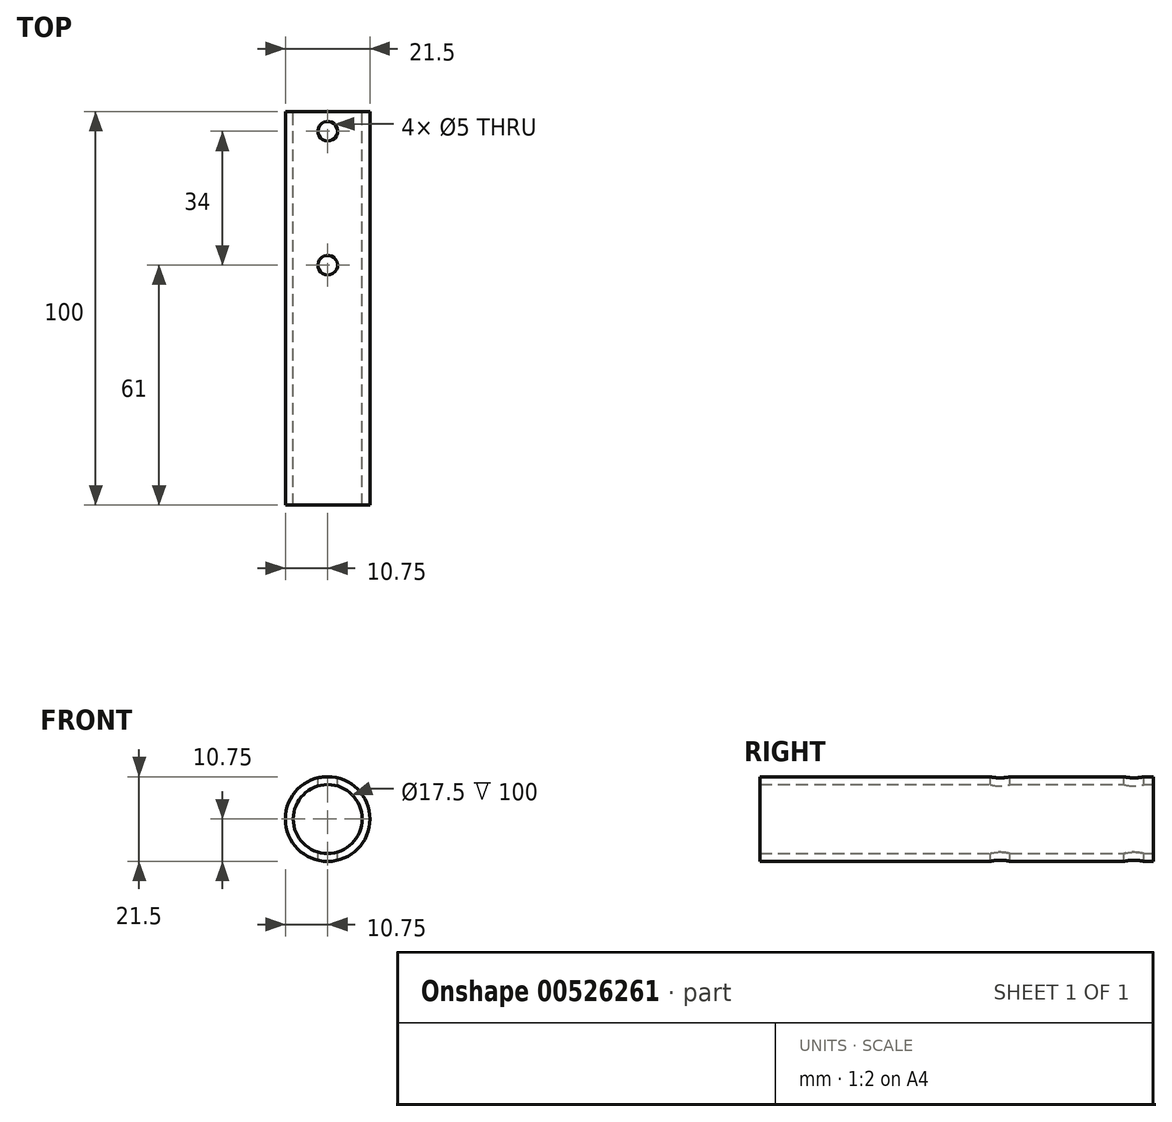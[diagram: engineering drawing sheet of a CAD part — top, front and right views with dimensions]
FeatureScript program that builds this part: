
annotation { "Feature Type Name" : "Feature", "Feature Type Description" : "" }
export const myFeature = defineFeature(function(context is Context, id is Id, definition is map)
    precondition{}
    {
        {
            var Q0;
            Q0=qCreatedBy(makeId("Front.planeOp"),FACE);
            var sketch = newSketch(context, id + "F0", { "sketchPlane" : qUnion([Q0])});
            skCircle(sketch, "E0", {"center": v(0, 0) * mm, "radius": 10.75 * mm});
            skCircle(sketch, "E1", {"center": v(0, 0) * mm, "radius": 8.75 * mm});
            skSolve(sketch);
        }
        {
            var Q0;
            Q0 = qSketchRegion(id + "F0", true);
            extrude(context, id + "F1", {"entities" : qUnion([Q0]), "depth" : 100 * mm, "offsetDistance" : 25 * mm});
        }
        {
            var Q0;
            Q0=qCreatedBy(makeId("Top.planeOp"),FACE);
            var sketch = newSketch(context, id + "F2", { "sketchPlane" : qUnion([Q0])});
            skCircle(sketch, "E2", {"center": v(0, -5) * mm, "radius": 2.5 * mm});
            skCircle(sketch, "E3", {"center": v(0, -39) * mm, "radius": 2.5 * mm});
            skSolve(sketch);
        }
        {
            var Q0;
            Q0 = qSketchRegion(id + "F2", true);
            extrude(context, id + "F3", {"entities" : qUnion([Q0]), "operationType" : NewBodyOperationType.REMOVE, "endBound" : BoundingType.SYMMETRIC, "oppositeDirection" : true, "depth" : 50 * mm, "offsetDistance" : 25 * mm});
        }
    });
